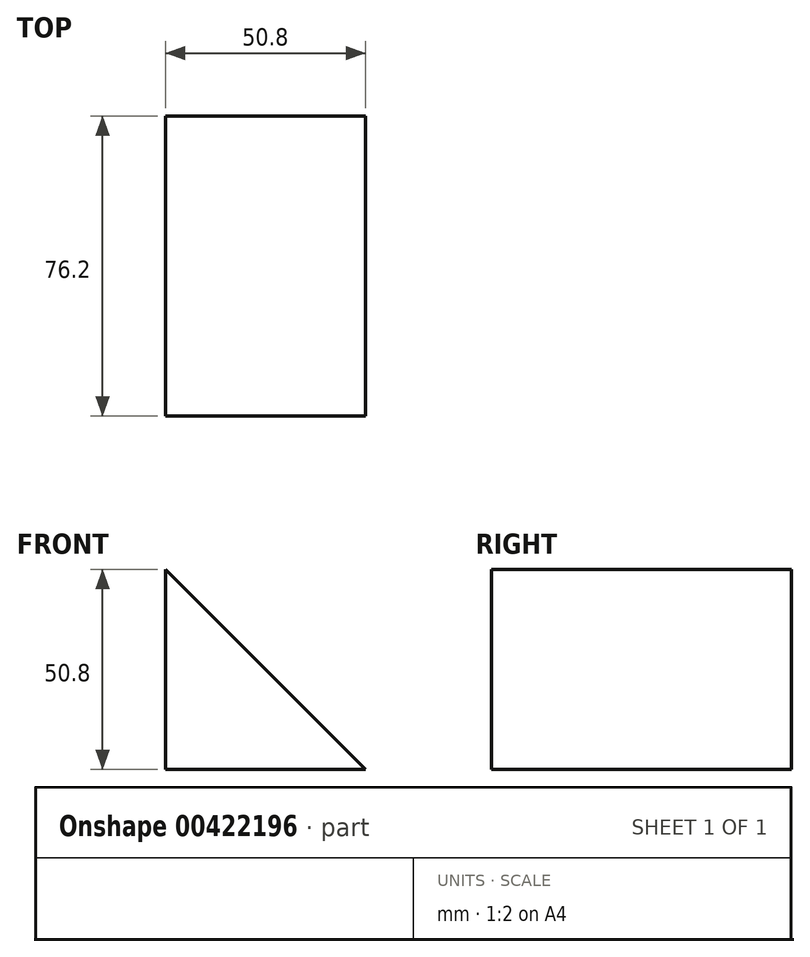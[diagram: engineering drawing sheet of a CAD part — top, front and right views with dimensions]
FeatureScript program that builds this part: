
annotation { "Feature Type Name" : "Feature", "Feature Type Description" : "" }
export const myFeature = defineFeature(function(context is Context, id is Id, definition is map)
    precondition{}
    {
        {
            var Q0;
            Q0=qCreatedBy(makeId("Front.planeOp"),FACE);
            var sketch = newSketch(context, id + "F0", { "sketchPlane" : qUnion([Q0])});
            skLineSegment(sketch, "E0", {"start": v(-29.03, 12.3) * mm, "end": v(-29.03, -38.5) * mm});
            skLineSegment(sketch, "E1", {"start": v(-29.03, -38.5) * mm, "end": v(21.77, -38.5) * mm});
            skLineSegment(sketch, "E2", {"start": v(21.77, -38.5) * mm, "end": v(-29.03, 12.3) * mm});
            skSolve(sketch);
        }
        {
            var Q0;
            Q0 = qSketchRegion(id + "F0", true);
            extrude(context, id + "F1", {"entities" : qUnion([Q0]), "depth" : 76.2 * mm});
        }
    });
